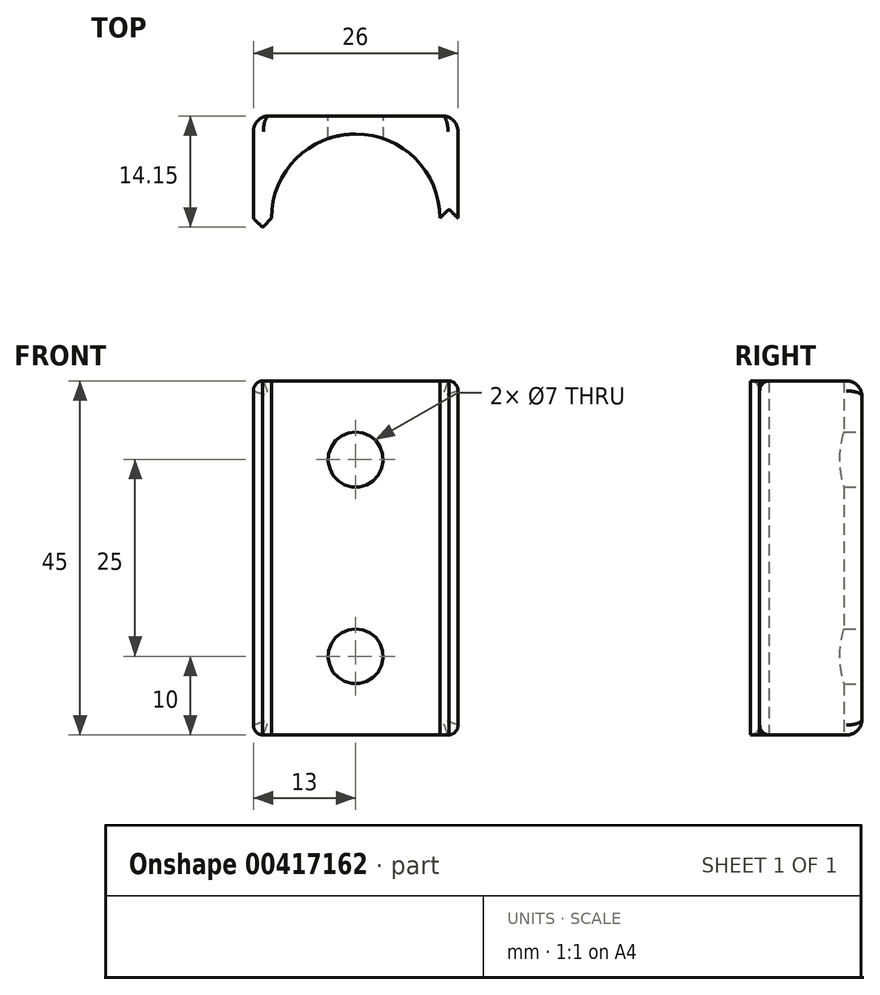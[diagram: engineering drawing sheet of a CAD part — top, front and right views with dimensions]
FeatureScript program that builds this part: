
annotation { "Feature Type Name" : "Feature", "Feature Type Description" : "" }
export const myFeature = defineFeature(function(context is Context, id is Id, definition is map)
    precondition{}
    {
        {
            var Q0;
            Q0=qCreatedBy(makeId("Top.planeOp"),FACE);
            var sketch = newSketch(context, id + "F0", { "sketchPlane" : qUnion([Q0])});
            skCircle(sketch, "E0", {"center": v(0, 0) * mm, "radius": 10.7 * mm});
            skLineSegment(sketch, "E1.bottom", {"start": v(13, -13) * mm, "end": v(-13, -13) * mm});
            skLineSegment(sketch, "E1.top", {"start": v(13, 13) * mm, "end": v(-13, 13) * mm});
            skLineSegment(sketch, "E1.left", {"start": v(13, -13) * mm, "end": v(13, 13) * mm});
            skLineSegment(sketch, "E1.right", {"start": v(-13, -13) * mm, "end": v(-13, 13) * mm});
            skLineSegment(sketch, "E2", {"start": v(-11.85, -1.15) * mm, "end": v(-13, 0) * mm});
            skLineSegment(sketch, "E3", {"start": v(-10.7, 0) * mm, "end": v(-11.85, -1.15) * mm});
            skLineSegment(sketch, "E4", {"start": v(11.85, 1.15) * mm, "end": v(10.7, 0) * mm});
            skLineSegment(sketch, "E5", {"start": v(11.85, 1.15) * mm, "end": v(13, 0) * mm});
            skLineSegment(sketch, "E6", {"start": v(-10.7, 0) * mm, "end": v(10.7, 0) * mm});
            skSolve(sketch);
        }
        {
            var Q0;
            {var subQ1=sQuery(id+"F0.wireOp",EDGE,"E1.top");Q0=makeQuery(id+"F0.imprint","IMPRINT",FACE,{"disambiguationData":[TD([[makeQuery(id+"F0.imprint","IMPRINT",EDGE,{"derivedFrom":subQ1}),1.0]])]});}
            extrude(context, id + "F1", {"entities" : qUnion([Q0]), "depth" : 45 * mm, "offsetDistance" : 25.4 * mm});
        }
        {
            var Q0;
            Q0=makeQuery(id+"F1.opExtrude","SWEPT_FACE",FACE,{"disambiguationData":[OSD([sQuery(id+"F0.wireOp",EDGE,"E1.top")])]});
            var sketch = newSketch(context, id + "F2", { "sketchPlane" : qUnion([Q0])});
            skLineSegment(sketch, "E7", {"start": v(0, 45) * mm, "end": v(0, 35) * mm});
            skPoint(sketch, "E7.endSnap0", {"position": v(0, 45) * mm});
            skLineSegment(sketch, "E8", {"start": v(0, 0) * mm, "end": v(0, 10) * mm});
            skPoint(sketch, "E8.endSnap0", {"position": v(0, 0) * mm});
            skCircle(sketch, "E9", {"center": v(0, 35) * mm, "radius": 3.5 * mm});
            skCircle(sketch, "E10", {"center": v(0, 10) * mm, "radius": 3.5 * mm});
            skSolve(sketch);
        }
        {
            var Q0;
            Q0=makeQuery(id+"F2.imprint","IMPRINT",FACE,{"disambiguationData":[TD([[makeQuery(id+"F2.imprint","IMPRINT",EDGE,{"derivedFrom":sQuery(id+"F2.wireOp",EDGE,"E9")}),1.0]])]});
            var Q1;
            Q1=makeQuery(id+"F2.imprint","IMPRINT",FACE,{"disambiguationData":[TD([[makeQuery(id+"F2.imprint","IMPRINT",EDGE,{"derivedFrom":sQuery(id+"F2.wireOp",EDGE,"E10")}),1.0]])]});
            extrude(context, id + "F3", {"entities" : qUnion([Q0, Q1]), "operationType" : NewBodyOperationType.REMOVE, "endBound" : BoundingType.UP_TO_NEXT, "oppositeDirection" : true, "depth" : 25.4 * mm});
        }
        {
            var Q0;
            Q0=makeQuery(id+"F1.opExtrude","SWEPT_EDGE",EDGE,{"disambiguationData":[OSD([sQuery(id+"F0.wireOp",EDGE,"E1.top"),sQuery(id+"F0.wireOp",EDGE,"E1.right")])]});
            var Q1;
            Q1=makeQuery(id+"F1.opExtrude","CAP_EDGE",EDGE,{"disambiguationData":[OSD([sQuery(id+"F0.wireOp",EDGE,"E1.top")])],"isStart":false});
            var Q2;
            Q2=makeQuery(id+"F1.opExtrude","SWEPT_EDGE",EDGE,{"disambiguationData":[OSD([sQuery(id+"F0.wireOp",EDGE,"E1.top"),sQuery(id+"F0.wireOp",EDGE,"E1.left")])]});
            var Q3;
            Q3=makeQuery(id+"F1.opExtrude","CAP_EDGE",EDGE,{"disambiguationData":[OSD([sQuery(id+"F0.wireOp",EDGE,"E1.top")])],"isStart":true});
            fillet(context, id + "F4", {"entities" : qUnion([Q0, Q1, Q2, Q3]), "radius" : 2 * mm, "tangentPropagation" : true, "allowEdgeOverflow" : false});
        }
        {
            var Q0;
            Q0=makeQuery(id+"F1.opExtrude","CAP_EDGE",EDGE,{"disambiguationData":[OSD([sQuery(id+"F0.wireOp",EDGE,"E1.left")])],"isStart":false});
            var Q1;
            Q1=makeQuery(id+"F1.opExtrude","CAP_EDGE",EDGE,{"disambiguationData":[OSD([sQuery(id+"F0.wireOp",EDGE,"E1.left")])],"isStart":true});
            var Q2;
            Q2=makeQuery(id+"F1.opExtrude","CAP_EDGE",EDGE,{"disambiguationData":[OSD([sQuery(id+"F0.wireOp",EDGE,"E1.right")])],"isStart":false});
            var Q3;
            Q3=makeQuery(id+"F1.opExtrude","CAP_EDGE",EDGE,{"disambiguationData":[OSD([sQuery(id+"F0.wireOp",EDGE,"E1.right")])],"isStart":true});
            fillet(context, id + "F5", {"entities" : qUnion([Q0, Q1, Q2, Q3]), "radius" : 1.27 * mm, "tangentPropagation" : true, "allowEdgeOverflow" : false});
        }
    });
